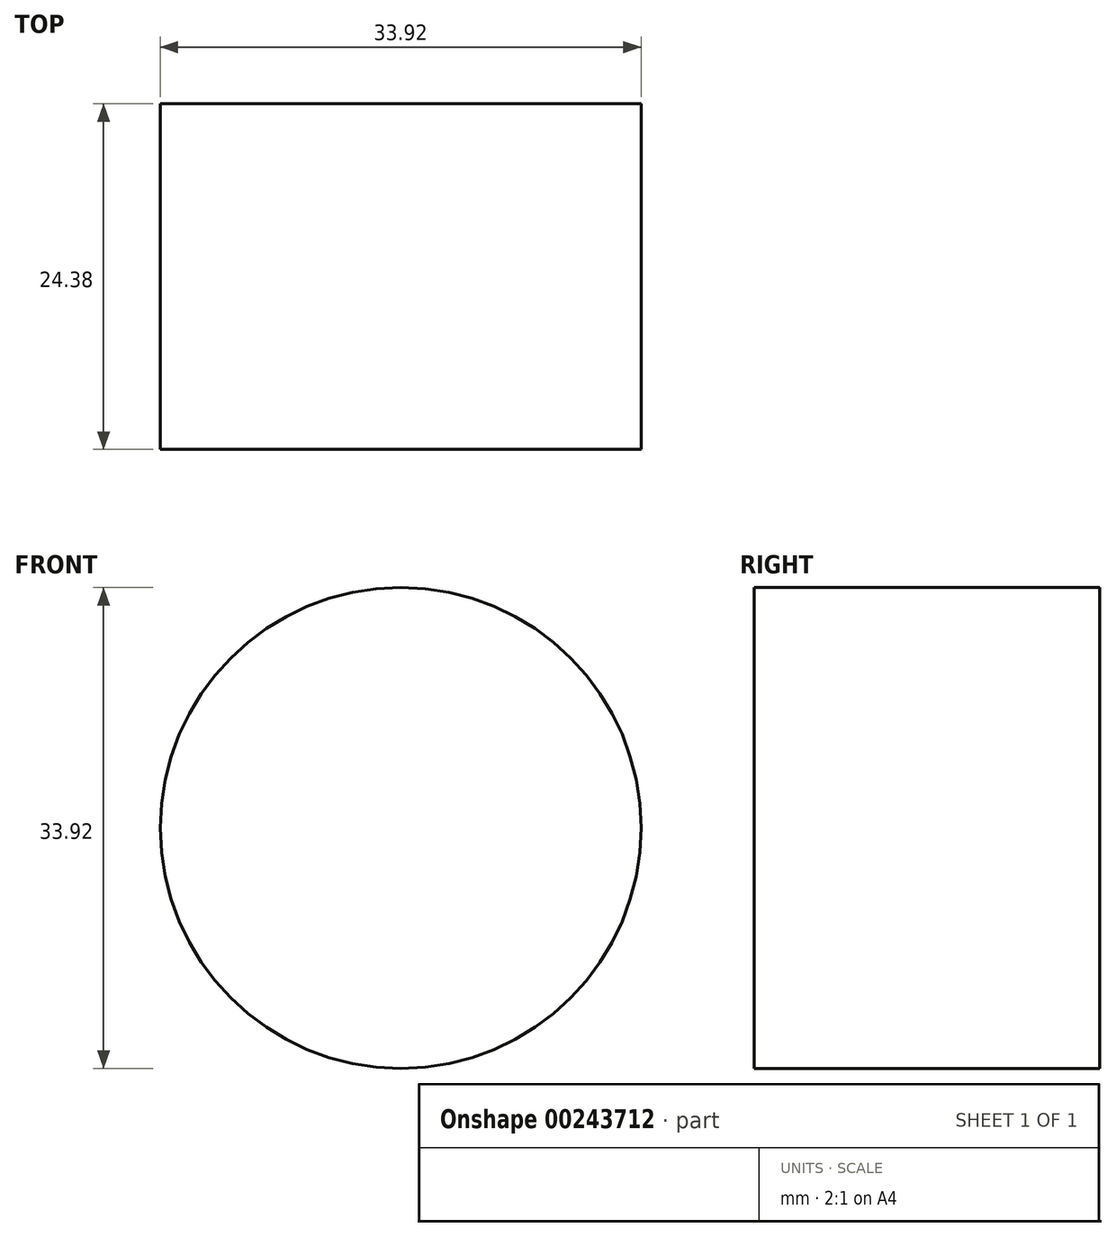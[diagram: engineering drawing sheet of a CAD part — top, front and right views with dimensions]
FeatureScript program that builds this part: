
annotation { "Feature Type Name" : "Feature", "Feature Type Description" : "" }
export const myFeature = defineFeature(function(context is Context, id is Id, definition is map)
    precondition{}
    {
        {
            var Q0;
            Q0=qCreatedBy(makeId("Front.planeOp"),FACE);
            var sketch = newSketch(context, id + "F0", { "sketchPlane" : qUnion([Q0])});
            skCircle(sketch, "E0", {"center": v(0, 0) * mm, "radius": 16.96 * mm});
            skSolve(sketch);
        }
        {
            var Q0;
            Q0=makeQuery(id+"F0.imprint","IMPRINT",FACE,{"disambiguationData":[TD([[makeQuery(id+"F0.imprint","IMPRINT",EDGE,{"derivedFrom":sQuery(id+"F0.wireOp",EDGE,"E0")}),1.0]])]});
            extrude(context, id + "F1", {"entities" : qUnion([Q0]), "oppositeDirection" : true, "depth" : 24.38 * mm});
        }
    });
